# Revit family: Mixer-Basin-Caroma Track Mini
name_source: partatom
category: Plumbing Fixtures
revit_build: Autodesk Revit 2014 (Build: 20131024_2115(x64)
units: mm (PartAtom-declared; Revit-internal decimal feet)

## types (1)
- Standard
    Assembly Code = D2020300
    CW Connection = Yes
    CWFU = 1.18
    Connector Radius = 10 mm  [stored 0.0328084 ft]
    Cost = 0 $
    Default Elevation = 0 mm  [stored 0 ft]
    Description = Track mixers and showers from Australia's leading bathroom brand will lift the feel of any bathroom. Choose the clean, contemporary European design without the European price.
    HW Connection = Yes
    HWFU = 1.18
    Height_ANZRS = 156 mm  [stored 0.511811 ft]
    Length_ANZRS = 44 mm  [stored 0.144357 ft]
    Manufacturer = GWA Bathrooms & Kitchens
    Material_ANZRS = Metal-Chrome-Caroma
    Model = 90216C6A
    ModifiedIssue_ANZRS = 20150112 $
    Type Comments = Caroma Track Mini Basin Mixer
    URL = http://specify.caroma.com.au
    Vent Connection = No
    WELSRating_ANZRS = WELS 6 Star rated, 4.5L/min
    Waste Connection = No
    Width_ANZRS = 153 mm  [stored 0.501969 ft]

note: [stored X ft] marks values corroborated as IEEE doubles in the binary element streams (Revit-internal decimal feet)

## geometry (parser evidence)
native form markers: Blend x10, Sweep x1
no freeform markers — native parametric forms only
